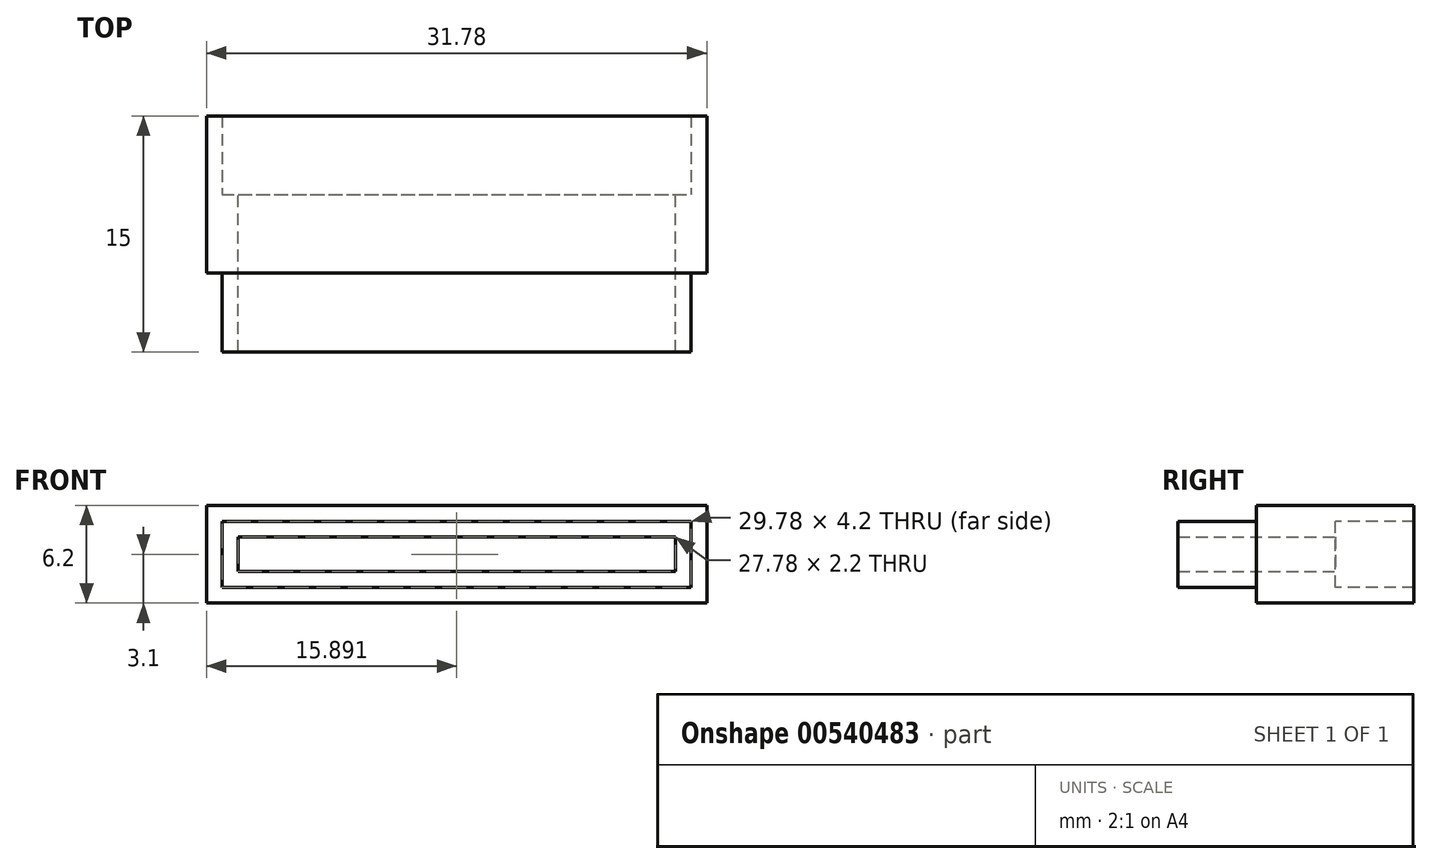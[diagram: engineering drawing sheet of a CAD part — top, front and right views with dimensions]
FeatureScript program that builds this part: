
annotation { "Feature Type Name" : "Feature", "Feature Type Description" : "" }
export const myFeature = defineFeature(function(context is Context, id is Id, definition is map)
    precondition{}
    {
        {
            var Q0;
            Q0=qCreatedBy(makeId("Front.planeOp"),FACE);
            var sketch = newSketch(context, id + "F0", { "sketchPlane" : qUnion([Q0])});
            skLineSegment(sketch, "E0", {"start": v(-16, -3.1) * mm, "end": v(15.78, -3.1) * mm});
            skLineSegment(sketch, "E1", {"start": v(15.78, -3.1) * mm, "end": v(15.78, 3.1) * mm});
            skLineSegment(sketch, "E2", {"start": v(15.78, 3.1) * mm, "end": v(-16, 3.1) * mm});
            skLineSegment(sketch, "E3", {"start": v(-16, 3.1) * mm, "end": v(-16, -3.1) * mm});
            skLineSegment(sketch, "E4.bottom", {"start": v(-15, -2.1) * mm, "end": v(14.78, -2.1) * mm});
            skLineSegment(sketch, "E4.top", {"start": v(-15, 2.1) * mm, "end": v(14.78, 2.1) * mm});
            skLineSegment(sketch, "E4.left", {"start": v(-15, -2.1) * mm, "end": v(-15, 2.1) * mm});
            skLineSegment(sketch, "E4.right", {"start": v(14.78, -2.1) * mm, "end": v(14.78, 2.1) * mm});
            skLineSegment(sketch, "E5.bottom", {"start": v(-14, 1.1) * mm, "end": v(13.78, 1.1) * mm});
            skLineSegment(sketch, "E5.top", {"start": v(-14, -1.1) * mm, "end": v(13.78, -1.1) * mm});
            skLineSegment(sketch, "E5.left", {"start": v(-14, 1.1) * mm, "end": v(-14, -1.1) * mm});
            skLineSegment(sketch, "E5.right", {"start": v(13.78, 1.1) * mm, "end": v(13.78, -1.1) * mm});
            skSolve(sketch);
        }
        {
            var Q0;
            Q0=makeQuery(id+"F0.imprint","IMPRINT",FACE,{"disambiguationData":[TD([[makeQuery(id+"F0.imprint","IMPRINT",EDGE,{"derivedFrom":sQuery(id+"F0.wireOp",EDGE,"E0")}),1.0]])]});
            extrude(context, id + "F1", {"entities" : qUnion([Q0]), "oppositeDirection" : true, "depth" : 5 * mm, "offsetDistance" : 25 * mm, "hasSecondDirection" : true, "secondDirectionOppositeDirection" : false, "secondDirectionDepth" : 5 * mm});
        }
        {
            var Q0;
            Q0=makeQuery(id+"F0.imprint","IMPRINT",FACE,{"disambiguationData":[TD([[makeQuery(id+"F0.imprint","IMPRINT",EDGE,{"derivedFrom":sQuery(id+"F0.wireOp",EDGE,"E4.bottom")}),1.0]])]});
            extrude(context, id + "F2", {"entities" : qUnion([Q0]), "operationType" : NewBodyOperationType.ADD, "depth" : 10 * mm, "offsetDistance" : 25 * mm});
        }
    });
